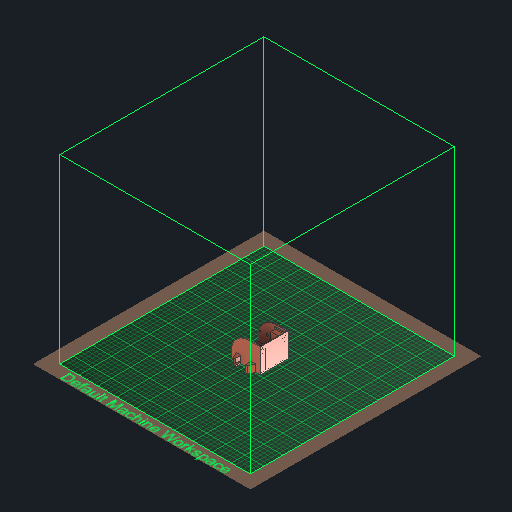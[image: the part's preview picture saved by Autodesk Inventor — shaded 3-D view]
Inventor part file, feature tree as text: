
AUTODESK INVENTOR PART (.ipt)
format: ipt  version: 2022 (Build 260153000, 153)  size: 519,680 bytes
history: native  units: in
note: dims shown in document units (in); Inventor stores cm internally (conversion verified against a paired STEP export)
features: extrude x9, sketch x8, projected_geometry x7, chamfer x3, reference x3, other x3, fillet x1
ambient origin geometry x8: Origin, YZ Plane, XZ Plane, XY Plane, X Axis, Y Axis, Z Axis, Center Point
bodies: Solid1 (feature_tree)
feature tree (34):
  extrude  "Extrusion1"  Depth=2.25in
  extrude  "Extrusion2"  TaperAngle=0.0deg  [1 undecoded]
  fillet  "Fillet1"  Radius=0.05in
  extrude  "Extrusion3"  Depth=0.1in
  extrude  "Extrusion4"  Depth=2.5in TaperAngle=0.0deg
  extrude  "Extrusion5"  Depth=0.1in
  extrude  "Extrusion6"  Depth=0.1in
  chamfer  "Chamfer3"  Distance=0.1in
  chamfer  "Chamfer4"  Distance=0.1in
  extrude  "Extrusion7"  Depth=0.1in
  extrude  "Extrusion8"  Depth=0.25in
  chamfer  "Chamfer5"  Distance=0.1in
  extrude  "Extrusion9"  Depth=1.0in TaperAngle=0.0deg
  sketch  "Sketch1"  dims[d0=2.0in d1=2.25in]
  sketch  "Sketch2"  dims[d2=0.8in d3=0.0in d4=0.05in d5=0.0in]
  projected_geometry  "Projected Loop1"
  projected_geometry  "Projected Loop2"
  projected_geometry  "Projected Loop3"
  projected_geometry  "Projected Loop4"
  sketch  "Sketch4"  dims[d6=0.1in d7=0.1in]
  reference  "Reference1"
  reference  "Reference2"
  reference  "Reference3"
  sketch  "Sketch5"  dims[d8=0.1in d9=2.5in d10=0.0in]
  projected_geometry  "Projected Loop5"
  sketch  "Sketch6"  dims[d11=1.5in d12=0.1in]
  sketch  "Sketch8"  dims[d13=0.1in d14=0.1in]
  sketch  "Sketch9"  dims[d15=0.25in]
  projected_geometry  "Projected Loop6"
  sketch  "Sketch10"  dims[d16=0.1in d17=0.1in d18=0.1in d19=0.1in d20=0.25in d21=0.1in d22=1.0in d23=0.0in d26=0.5in d27=0.0in d28=2.25in d30=0.25in d31=0.1in d32=0.0in d33=0.0in d34=0.0in d38=0.2in d39=0.1in d40=0.0in d41=0.95in d42=1.75in d46=0.5in d47=0.125in d48=0.1718in d49=0.5in d50=0.125in d51=0.1718in d52=0.1111in d53=0.25in d54=0.5in d55=0.0in d56=0.25in d57=0.25in d58=0.25in d59=0.16in d60=0.125in d61=0.125in d62=1.0in d63=0.0in d64=0.25in d65=0.125in d66=45.0deg d67=0.285in d68=45.0deg d69=0.1in d70=0.0in d29=0.0344in]
  projected_geometry  "Projected Loop7"
  parser-record x1  (decoder bookkeeping rows leaked as tree rows — omitted from the tree; the rows remain in map.json)
  other  "Prototype Assembly.iam"
  other  "ServoMotor:1"
note: 1 required parameter value undecoded (feature->parameter linkage not recoverable at this tier; creation-order binding heuristic only, values carry confidence <= 0.55)
note: 1 file-system path scrubbed to <path> (originals preserved in map.json)
